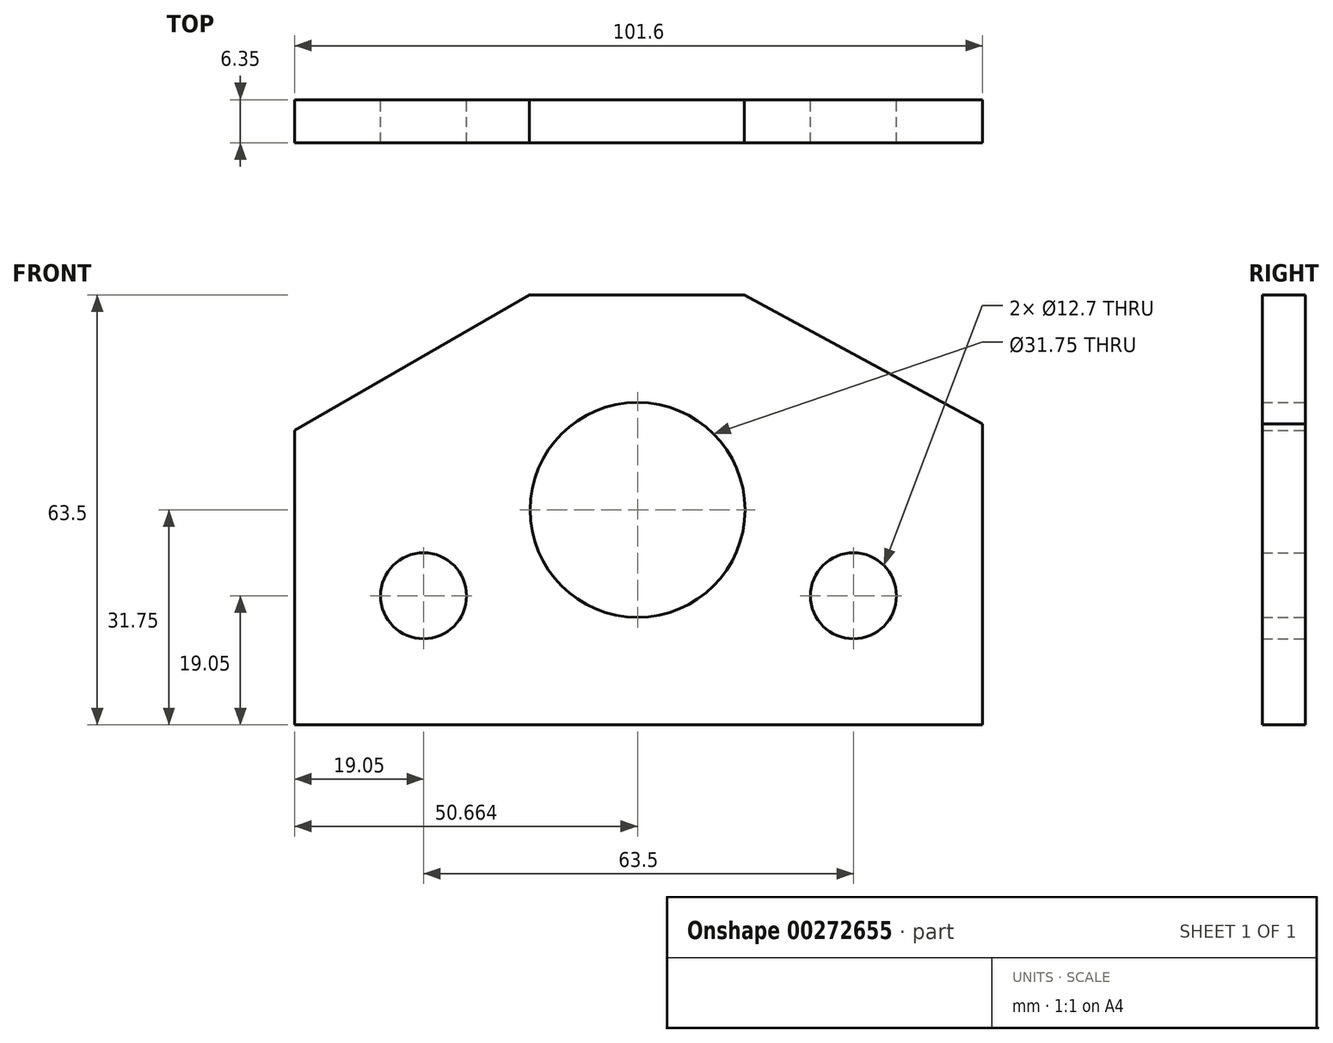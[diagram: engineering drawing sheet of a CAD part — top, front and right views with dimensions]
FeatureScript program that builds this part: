
annotation { "Feature Type Name" : "Feature", "Feature Type Description" : "" }
export const myFeature = defineFeature(function(context is Context, id is Id, definition is map)
    precondition{}
    {
        {
            var Q0;
            Q0=qCreatedBy(makeId("Front.planeOp"),FACE);
            var sketch = newSketch(context, id + "F0", { "sketchPlane" : qUnion([Q0])});
            skLineSegment(sketch, "E0", {"start": v(-65.62, 0) * mm, "end": v(35.98, 0) * mm});
            skLineSegment(sketch, "E1", {"start": v(-65.62, 0) * mm, "end": v(-65.62, 43.48) * mm});
            skLineSegment(sketch, "E2", {"start": v(35.98, 0) * mm, "end": v(35.98, 44.45) * mm});
            skLineSegment(sketch, "E3", {"start": v(35.98, 44.45) * mm, "end": v(0.78, 63.5) * mm});
            skLineSegment(sketch, "E4", {"start": v(0.78, 63.5) * mm, "end": v(-30.97, 63.5) * mm});
            skLineSegment(sketch, "E5", {"start": v(-30.97, 63.5) * mm, "end": v(-65.62, 43.48) * mm});
            skLineSegment(sketch, "E6", {"start": v(-14.82, 0) * mm, "end": v(-15.1, 63.5) * mm, "construction": true});
            skPoint(sketch, "E6.endSnap0", {"position": v(-15.1, 63.5) * mm});
            skCircle(sketch, "E7", {"center": v(-14.96, 31.75) * mm, "radius": 15.88 * mm});
            skCircle(sketch, "E8", {"center": v(-46.57, 19.05) * mm, "radius": 6.35 * mm});
            skCircle(sketch, "E9", {"center": v(16.93, 19.05) * mm, "radius": 6.35 * mm});
            skSolve(sketch);
        }
        {
            var Q0;
            Q0=makeQuery(id+"F0.imprint","IMPRINT",FACE,{"disambiguationData":[TD([[makeQuery(id+"F0.imprint","IMPRINT",EDGE,{"derivedFrom":sQuery(id+"F0.wireOp",EDGE,"E0")}),1.0]])]});
            extrude(context, id + "F1", {"entities" : qUnion([Q0]), "depth" : 6.35 * mm});
        }
    });
